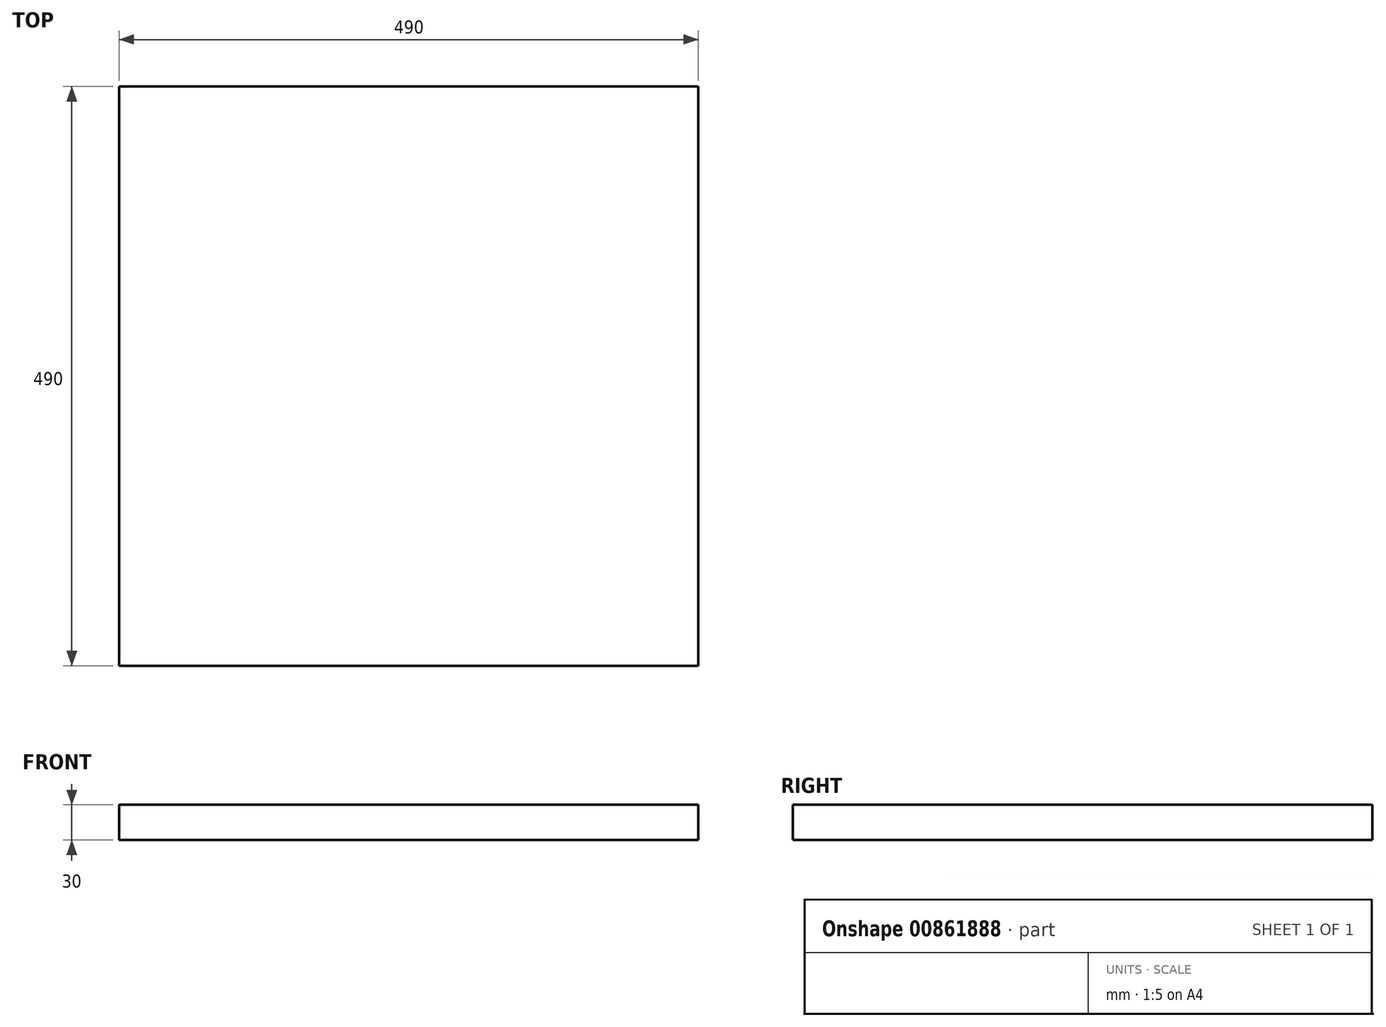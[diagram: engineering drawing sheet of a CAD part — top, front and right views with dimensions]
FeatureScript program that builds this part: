
annotation { "Feature Type Name" : "Feature", "Feature Type Description" : "" }
export const myFeature = defineFeature(function(context is Context, id is Id, definition is map)
    precondition{}
    {
        {
            var Q0;
            Q0=qCreatedBy(makeId("Top.planeOp"),FACE);
            var sketch = newSketch(context, id + "F0", { "sketchPlane" : qUnion([Q0])});
            skLineSegment(sketch, "E0.bottom", {"start": v(-245, -245) * mm, "end": v(245, -245) * mm});
            skLineSegment(sketch, "E0.top", {"start": v(-245, 245) * mm, "end": v(245, 245) * mm});
            skLineSegment(sketch, "E0.left", {"start": v(-245, -245) * mm, "end": v(-245, 245) * mm});
            skLineSegment(sketch, "E0.right", {"start": v(245, -245) * mm, "end": v(245, 245) * mm});
            skPoint(sketch, "E0.middle", {"position": v(0, 0) * mm});
            skSolve(sketch);
        }
        {
            var Q0;
            Q0=makeQuery(id+"F0.imprint","IMPRINT",FACE,{"disambiguationData":[TD([[makeQuery(id+"F0.imprint","IMPRINT",EDGE,{"derivedFrom":sQuery(id+"F0.wireOp",EDGE,"E0.bottom")}),1.0]])]});
            extrude(context, id + "F1", {"entities" : qUnion([Q0]), "depth" : 30 * mm, "offsetDistance" : 25 * mm});
        }
    });
